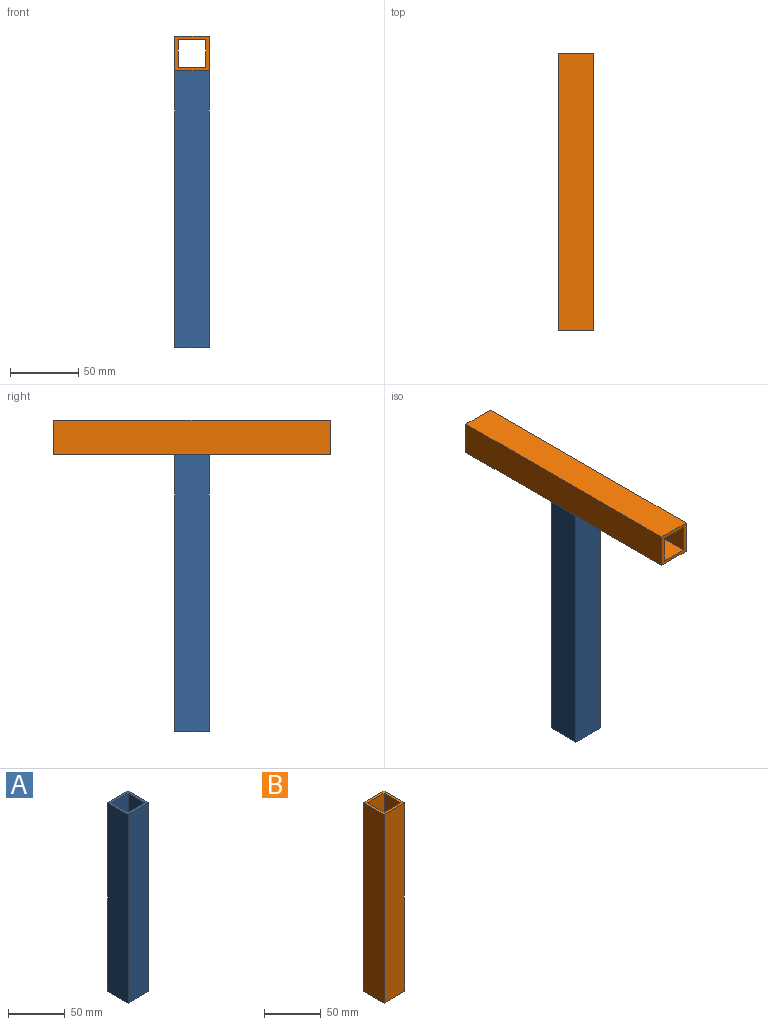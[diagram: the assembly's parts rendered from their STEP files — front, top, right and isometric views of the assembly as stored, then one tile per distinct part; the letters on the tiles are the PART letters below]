
ASSEMBLY  parts=2 mates=1
PART A: 10 faces, bbox 25.4x25.4x203.2 mm
  f0: plane 25.4x25.4mm, normal (0,0,-1), area 232.3mm2, adj f2,f3,f4,f5,f6,f7,f8,f9
  f1: plane 25.4x25.4mm, normal (0,0,1), area 232.3mm2, adj f2,f3,f4,f5,f6,f7,f8,f9
  f2: plane 203.2x25.4mm, normal (1,0,0), area 5161.3mm2, adj f0,f1,f4,f5
  f3: plane 203.2x25.4mm, normal (-1,0,0), area 5161.3mm2, adj f0,f1,f4,f5
  f4: plane 203.2x25.4mm, normal (0,-1,0), area 5161.3mm2, adj f0,f1,f2,f3
  f5: plane 203.2x25.4mm, normal (0,1,0), area 5161.3mm2, adj f0,f1,f2,f3
  f6: plane 203.2x20.32mm, normal (-1,0,0), area 4129mm2, adj f0,f1,f8,f9
  f7: plane 203.2x20.32mm, normal (1,0,0), area 4129mm2, adj f0,f1,f8,f9
  f8: plane 203.2x20.32mm, normal (0,1,0), area 4129mm2, adj f0,f1,f6,f7
  f9: plane 203.2x20.32mm, normal (0,-1,0), area 4129mm2, adj f0,f1,f6,f7
PART B: 10 faces, bbox 25.4x25.4x203.2 mm
  f0: plane 25.4x25.4mm, normal (0,0,1), area 232.3mm2, adj f2,f3,f4,f5,f6,f7,f8,f9
  f1: plane 25.4x25.4mm, normal (0,0,-1), area 232.3mm2, adj f2,f3,f4,f5,f6,f7,f8,f9
  f2: plane 203.2x25.4mm, normal (1,0,0), area 5161.3mm2, adj f0,f1,f4,f5
  f3: plane 203.2x25.4mm, normal (-1,0,0), area 5161.3mm2, adj f0,f1,f4,f5
  f4: plane 203.2x25.4mm, normal (0,-1,0), area 5161.3mm2, adj f0,f1,f2,f3
  f5: plane 203.2x25.4mm, normal (0,1,0), area 5161.3mm2, adj f0,f1,f2,f3
  f6: plane 203.2x20.32mm, normal (-1,0,0), area 4129mm2, adj f0,f1,f8,f9
  f7: plane 203.2x20.32mm, normal (1,0,0), area 4129mm2, adj f0,f1,f8,f9
  f8: plane 203.2x20.32mm, normal (0,1,0), area 4129mm2, adj f0,f1,f6,f7
  f9: plane 203.2x20.32mm, normal (0,-1,0), area 4129mm2, adj f0,f1,f6,f7
PLACE A t=(-17.14,-0.41,-6.99)mm
PLACE B rot(axis=(1,0,0),90deg) t=(46.23,-15.75,118.08)mm
MATE fastened B.f4 <-> A.f1  axis (0,0,-1) through (19.69,-13.11,92.68)mm
